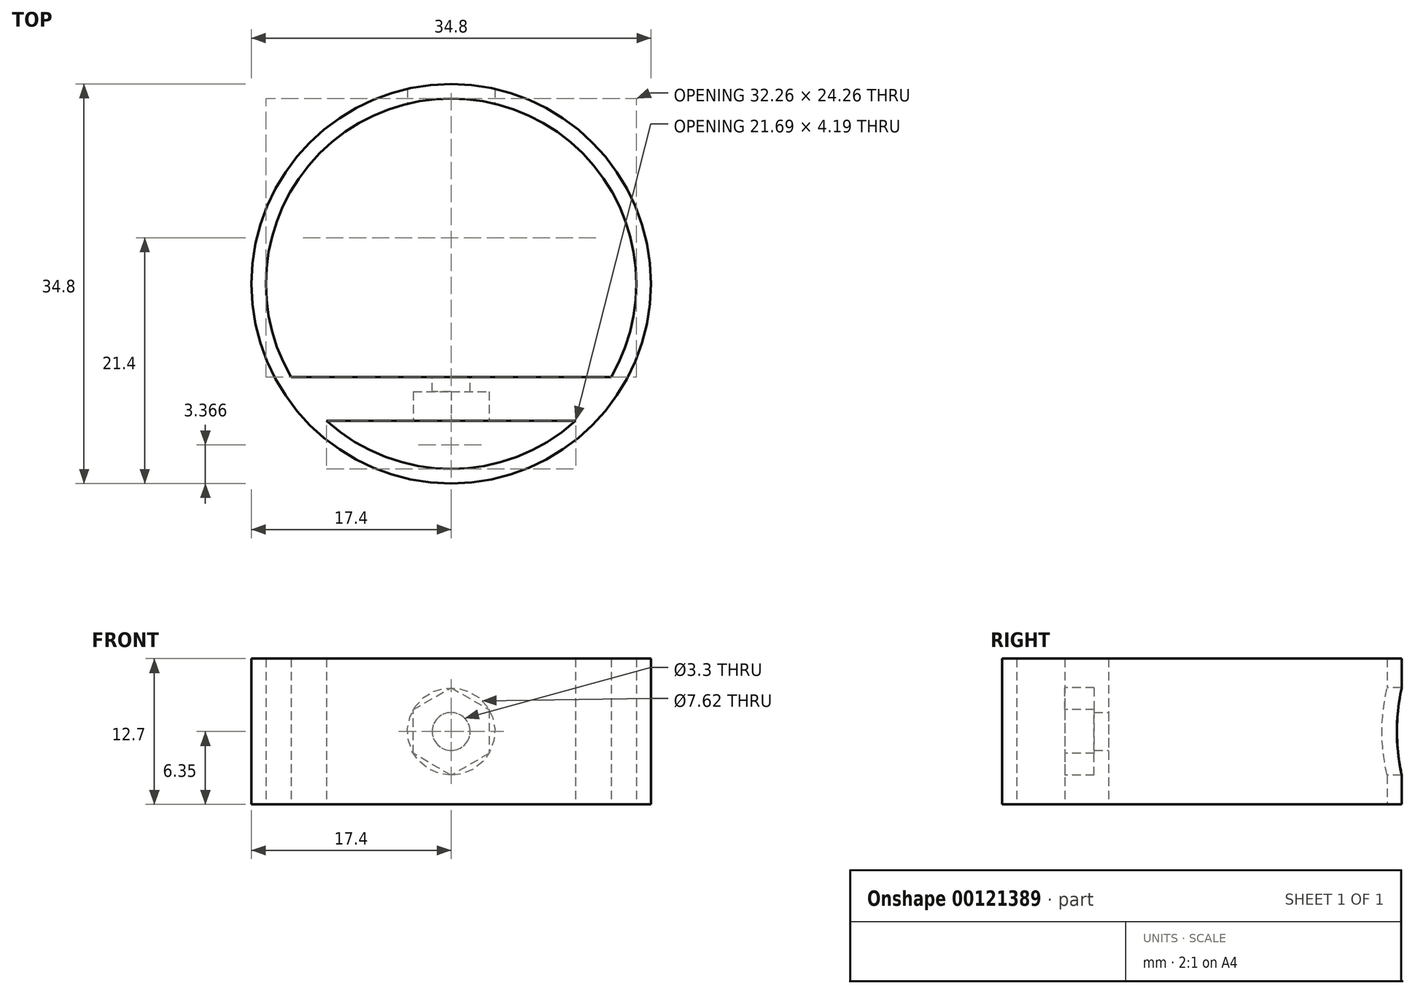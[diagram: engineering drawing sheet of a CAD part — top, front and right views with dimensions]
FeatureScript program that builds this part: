
annotation { "Feature Type Name" : "Feature", "Feature Type Description" : "" }
export const myFeature = defineFeature(function(context is Context, id is Id, definition is map)
    precondition{}
    {
        {
            var Q0;
            Q0=qCreatedBy(makeId("Top.planeOp"),FACE);
            var sketch = newSketch(context, id + "F0", { "sketchPlane" : qUnion([Q0])});
            skCircle(sketch, "E0", {"center": v(0, 0) * mm, "radius": 17.4 * mm});
            skLineSegment(sketch, "E1", {"start": v(-13.93, -8.13) * mm, "end": v(13.93, -8.13) * mm});
            skLineSegment(sketch, "E2", {"start": v(-10.85, -11.94) * mm, "end": v(10.85, -11.94) * mm});
            skArc(sketch, "E3", {"start": v(-13.93, -8.13) * mm, "mid": v(-12.53, -10.15) * mm, "end": v(-10.85, -11.94) * mm, "construction": true});
            skArc(sketch, "E4", {"start": v(-10.85, -11.94) * mm, "mid": v(0, -16.13) * mm, "end": v(10.85, -11.94) * mm});
            skArc(sketch, "E5", {"start": v(13.93, -8.13) * mm, "mid": v(0, 16.13) * mm, "end": v(-13.93, -8.13) * mm});
            skArc(sketch, "E6", {"start": v(10.85, -11.94) * mm, "mid": v(12.53, -10.15) * mm, "end": v(13.93, -8.13) * mm, "construction": true});
            skLineSegment(sketch, "E7", {"start": v(-13.93, -8.13) * mm, "end": v(-15.03, -8.77) * mm, "construction": true});
            skSolve(sketch);
        }
        {
            var Q0;
            Q0 = qSketchRegion(id + "F0", true);
            extrude(context, id + "F1", {"entities" : qUnion([Q0]), "depth" : 12.7 * mm});
        }
        {
            var Q0;
            Q0=makeQuery(id+"F1.opExtrude","SWEPT_FACE",FACE,{"disambiguationData":[OSD([sQuery(id+"F0.wireOp",EDGE,"E1")])]});
            var sketch = newSketch(context, id + "F2", { "sketchPlane" : qUnion([Q0])});
            skPoint(sketch, "E8", {"position": v(0, 0) * mm});
            skPoint(sketch, "E9", {"position": v(-13.93, 6.35) * mm});
            skCircle(sketch, "E10", {"center": v(0, 6.35) * mm, "radius": 1.65 * mm});
            skSolve(sketch);
        }
        {
            var Q0;
            Q0 = qSketchRegion(id + "F2", true);
            var Q1;
            Q1=makeQuery(id+"F1.opExtrude","SWEPT_FACE",FACE,{"disambiguationData":[OSD([sQuery(id+"F0.wireOp",EDGE,"E2")])]});
            extrude(context, id + "F3", {"entities" : qUnion([Q0]), "operationType" : NewBodyOperationType.REMOVE, "endBound" : BoundingType.UP_TO_SURFACE, "oppositeDirection" : true, "endBoundEntityFace" : qUnion([Q1]), "depth" : 25.4 * mm});
        }
        {
            var Q0;
            Q0=makeQuery(id+"F1.opExtrude","SWEPT_FACE",FACE,{"disambiguationData":[OSD([sQuery(id+"F0.wireOp",EDGE,"E2")])]});
            var sketch = newSketch(context, id + "F4", { "sketchPlane" : qUnion([Q0])});
            skCircle(sketch, "E11.cCircle", {"center": v(0, 6.35) * mm, "radius": 3.3 * mm, "construction": true});
            skLineSegment(sketch, "E11.0", {"start": v(3.3, 8.26) * mm, "end": v(3.3, 4.44) * mm});
            skLineSegment(sketch, "E11.1", {"start": v(3.3, 4.44) * mm, "end": v(0, 2.54) * mm});
            skLineSegment(sketch, "E11.2", {"start": v(0, 2.54) * mm, "end": v(-3.3, 4.44) * mm});
            skLineSegment(sketch, "E11.3", {"start": v(-3.3, 4.44) * mm, "end": v(-3.3, 8.26) * mm});
            skLineSegment(sketch, "E11.4", {"start": v(-3.3, 8.26) * mm, "end": v(0, 10.16) * mm});
            skLineSegment(sketch, "E11.5", {"start": v(0, 10.16) * mm, "end": v(3.3, 8.26) * mm});
            skPoint(sketch, "E11.0.midPoint", {"position": v(3.3, 6.35) * mm});
            skSolve(sketch);
        }
        {
            var Q0;
            Q0 = qSketchRegion(id + "F4", true);
            extrude(context, id + "F5", {"entities" : qUnion([Q0]), "operationType" : NewBodyOperationType.REMOVE, "oppositeDirection" : true, "depth" : 2.54 * mm});
        }
        {
            var Q0;
            Q0=makeQuery(id+"F1.opExtrude","SWEPT_FACE",FACE,{"disambiguationData":[OSD([sQuery(id+"F0.wireOp",EDGE,"E1")])]});
            var sketch = newSketch(context, id + "F6", { "sketchPlane" : qUnion([Q0])});
            skCircle(sketch, "E12", {"center": v(0, 6.35) * mm, "radius": 3.81 * mm});
            skSolve(sketch);
        }
        {
            var Q0;
            Q0 = qSketchRegion(id + "F6", true);
            extrude(context, id + "F7", {"entities" : qUnion([Q0]), "operationType" : NewBodyOperationType.REMOVE, "endBound" : BoundingType.THROUGH_ALL, "depth" : 25.4 * mm});
        }
    });
